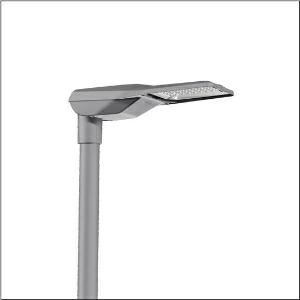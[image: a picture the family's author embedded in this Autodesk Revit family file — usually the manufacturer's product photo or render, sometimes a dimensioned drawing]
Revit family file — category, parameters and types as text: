
# Revit family: streetlight_sl_21_iq_mini___p0_8a_5xe2u31d08gb_8910
name_source: partatom
category: Lighting Fixtures
units: mm (PartAtom-declared; Revit-internal decimal feet)

## family parameters
Cut with Voids When Loaded = No
Host = Face
Light Source = No
Part Type = Normal
Room Calculation Point = No
Round Connector Dimension = Use Diameter
Shared = No

## types (1)
- --- (1 x LED, 5730 lm, 37.1 W, 3000K)
    Apparent Load = 37 VA
    CIE Flux Codes = 33 69 96 100 100
    Color Rendering = 70
    Color Temperature = 3000K
    Default Elevation = 1800 mm
    Description = Streetlight SL 21 iQ mini, mast luminaire, primary light control with lens, of PMMA, primary optical cover: cover, of toughened safety glass, transparent, light distribution: P0.8a, light emission: direct distribution, primary light characteristic: asymmetric, installation type: post-top, side-entry, LED, High Power LED, rated luminous flux: 5.730lm, luminous efficacy: 154lm/W, light colour: 730, colour temperature: 3000K, control gear: iQ-Comfort, control: pre-setting: linear dimming characteristic, Auto-Match, Temp-Guard, Lumen-Switch, Night-Set, Smart-Wire, Light-Fading, Desk-Remote (wireless, voltage-free reading and setting of iQ features in the workshop via application-optimized NFC function/RFID function), optimised constant luminous flux control (CLO 2.0), mains connection: 220..240V, AC, 50/60Hz, start of lifetime: 37W, end of service life: 39W, reduction: 18W, luminaire housing, of diecast aluminium, powder-coated, SITECO metallic grey (DB 702S), corrosivity category C5 high according to DIN EN ISO 12944, please order mast flange separately, inclination adjustable: 0°, 5°, 10°, 15°, sealing non-destructively replaceable, multi-level sealing system, length: 628mm, width: 235mm, height: 110mm, mast flange for spigot size: 42mm (side-entry): 5XC10008XM4, 60/48mm (side-entry/post-top): 5XC10108XM2, 76/60mm (side-entry/post-top): 5XC10108XM1, mounting height: 4..8m, protection rating (complete): IP66, insulation class (complete): insulation class II (safety insulation), certification: CE, ENEC, ENEC+, VDE, impact resistance: IK10, permissible operating ambient temperature for outdoor applications: -40..+50°C, standard-compliant lighting for roads and squares, packaging unit: 1 piece

Light Distribution: P0.8a
    Height = 110 mm
    Lamp = 1 x LED
    Lamp Light Flux = 5730 lm
    Lamp Power = 37.1 W
    Lamp count = 1
    Length = 625 mm
    Luminous efficacy = 154 lm/W
    Manufacturer = Siteco
    ModVariant = No
    Model = 5XE2U31D08GB
    Mounting Place = Pole
    Mounting Type = Pole top
    Number of Poles = 1
    OnlyDefault = Yes
    Power Factor = 1
    Product Name = Streetlight SL 21 iQ mini | P0.8a
    Product group = mast luminaire | pylon top
    ProductGroupID = 6100
    Protection Class = Protection class II
    Protection Degree = IP 66
    RLX_Detail_Level = 1
    RLX_Emergency_Light_Flux = 0 lm
    RLX_Emergency_Type = 0
    RLX_Emergency_Type_DB = No
    RlxData = <blob elided: 91993 chars, md5=a41c983d>
    Socket = socket
    Standby Power = 0 W
    System Light Flux = 5730 lm
    System Power = 37 W
    Type Comments = factory setting: luminous flux: 100 % | dim-lin: 254 | 385 mA
    Type Image = l_1003519.jpg
    URL = http://relux.com
    VarID = @adj_082041
    Voltage = 0 V
    Weight = 0.00 kg
    Width = 234 mm

## geometry (parser evidence)
native form markers: Blend x4, Sweep x10
no freeform markers — native parametric forms only
